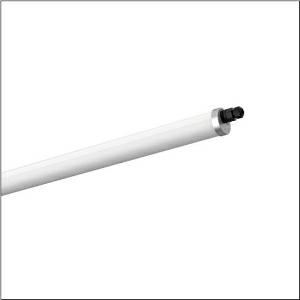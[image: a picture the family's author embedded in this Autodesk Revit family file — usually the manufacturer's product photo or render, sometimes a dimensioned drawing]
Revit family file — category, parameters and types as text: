
# Revit family: monsun_r__31_tube_51ft107n4a0a_c9dd
name_source: partatom
category: Lighting Fixtures
units: mm (PartAtom-declared; Revit-internal decimal feet)

## family parameters
Cut with Voids When Loaded = No
Host = Face
Light Source = No
Part Type = Normal
Room Calculation Point = No
Round Connector Dimension = Use Diameter
Shared = No

## types (1)
- Monsun® 31 Tube (1 x LED, 10000 lm, 58 W, 4000K)
    Apparent Load = 58 VA
    CIE Flux Codes = 42 71 90 91 100
    Color Rendering = 80
    Color Temperature = 4000K
    Default Elevation = 1800 mm
    Description = Monsun® 31 Tube, tubular luminaire, primary optical cover: diffuser, of PMMA, light emission: direct distribution, primary light characteristic: symmetric, installation type: suspended mounting, surface-mounted, LED, rated luminous flux: 10.000lm, luminous efficacy: 160lm/W, light colour: 840, colour temperature: 4000K, with with 1 terminal, 3-pole, max. 2.5mm², through-wiring: 3x 1.5mm², mains connection: 220..240V, AC, 50/60Hz, rated input power: 62W, housing, cylindrical, of PMMA, semi-transparent, matt white, length: 1.560mm, diameter: 75mm, end cap, of stainless steel (V2A), protection rating (complete): IP67/IP69K, insulation class (complete): insulation class I (protective earthing), certification: CE, UKCA, impact resistance: IK07, permissible operating ambient temperature: -20..+40°C, corresponds to IFS (International Featured Standards) requirements for safety and quality in the food industry, packaging unit: 1 piece
    Height = 83 mm
    Lamp = 1 x LED
    Lamp Light Flux = 10000 lm
    Lamp Power = 58 W
    Lamp count = 1
    Length = 1560 mm
    Luminous efficacy = 172 lm/W
    Manufacturer = Siteco
    ModVariant = No
    Model = 51FT107N4A0A
    Mounting Place = Ceiling
    Mounting Type = Pendant
    Number of Poles = 1
    OnlyDefault = Yes
    Power Factor = 1
    Product Name = Monsun® 31 Tube
    Product group = tubular luminaire
    ProductGroupID = 907
    Protection Class = Protection class I
    RLX_Detail_Level = 1
    RlxData = <blob elided: 24905 chars, md5=fa8da239>
    Socket = socket
    Standby Power = 0 W
    System Light Flux = 10000 lm
    System Power = 58 W
    Type Comments = Product without accessories
    Type Image = l_1228461.jpg
    URL = http://relux.com
    VarID = ---
    Voltage = 0 V
    Weight = 0.00 kg
    Width = 75 mm

## geometry (parser evidence)
native form markers: Blend x4, Sweep x15
no freeform markers — native parametric forms only
